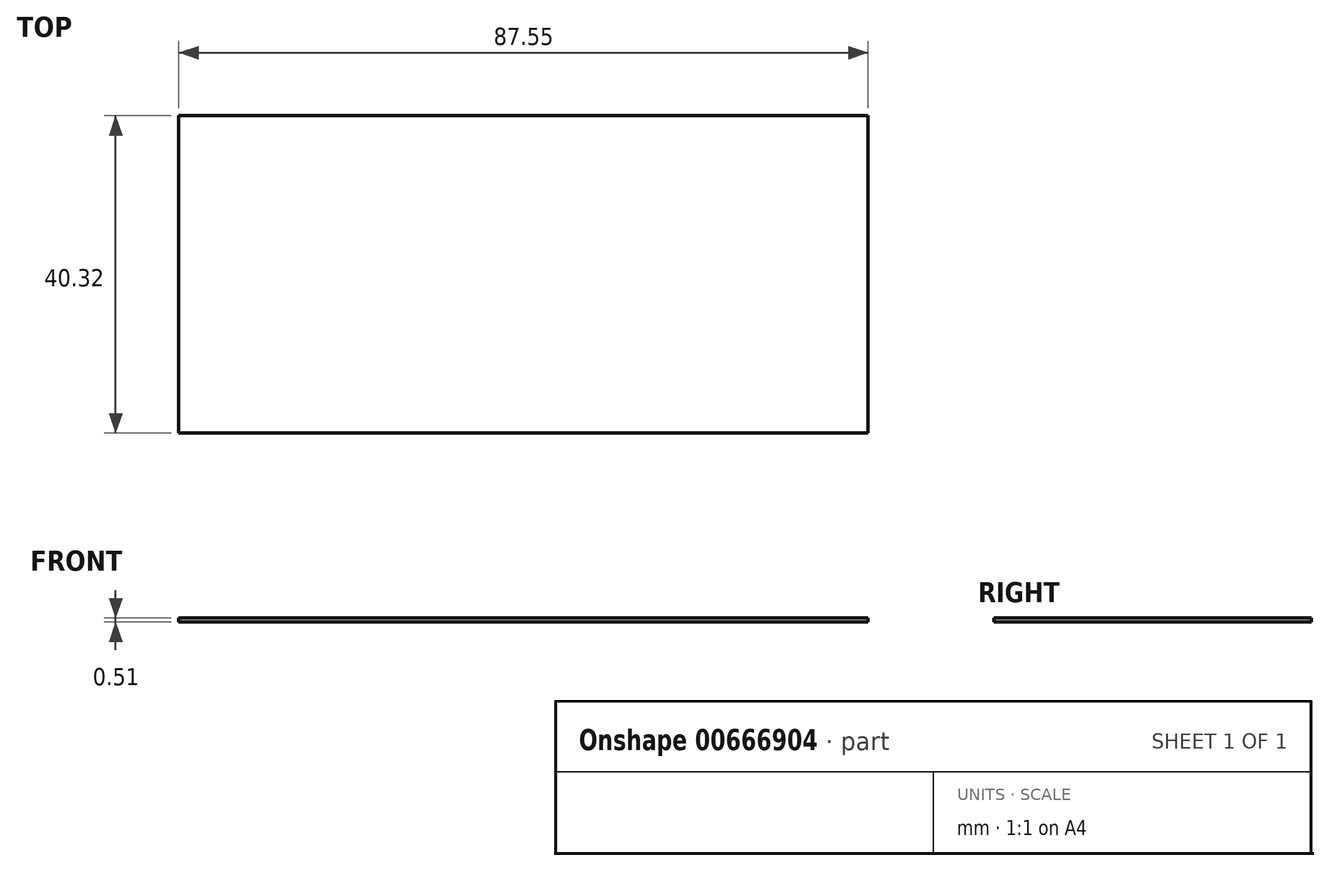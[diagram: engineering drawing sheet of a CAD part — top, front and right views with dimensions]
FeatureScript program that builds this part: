
annotation { "Feature Type Name" : "Feature", "Feature Type Description" : "" }
export const myFeature = defineFeature(function(context is Context, id is Id, definition is map)
    precondition{}
    {
        {
            var Q0;
            Q0=qCreatedBy(makeId("Top.planeOp"),FACE);
            var sketch = newSketch(context, id + "F0", { "sketchPlane" : qUnion([Q0])});
            skLineSegment(sketch, "E0.bottom", {"start": v(14.22, -10.64) * mm, "end": v(-73.33, -10.64) * mm});
            skLineSegment(sketch, "E0.top", {"start": v(14.22, 50.2) * mm, "end": v(-73.33, 50.2) * mm});
            skLineSegment(sketch, "E0.left", {"start": v(14.22, -10.64) * mm, "end": v(14.22, 50.2) * mm});
            skLineSegment(sketch, "E0.right", {"start": v(-73.33, -10.64) * mm, "end": v(-73.33, 50.2) * mm});
            skPoint(sketch, "E0.middle", {"position": v(-29.56, 19.79) * mm});
            skLineSegment(sketch, "E1", {"start": v(-73.33, 39.32) * mm, "end": v(14.22, 39.32) * mm});
            skLineSegment(sketch, "E2", {"start": v(-73.33, 29.68) * mm, "end": v(14.22, 29.68) * mm});
            skSolve(sketch);
        }
        {
            var Q0;
            Q0=makeQuery(id+"F0.imprint","IMPRINT",FACE,{"disambiguationData":[TD([[makeQuery(id+"F0.imprint","IMPRINT",EDGE,{"derivedFrom":sQuery(id+"F0.wireOp",EDGE,"E0.bottom")}),-1.0]])]});
            extrude(context, id + "F1", {"entities" : qUnion([Q0]), "depth" : 0.5 * mm, "offsetDistance" : 25.4 * mm, "hasSecondDirection" : true, "secondDirectionOppositeDirection" : false, "secondDirectionDepth" : 0 * mm});
        }
    });
